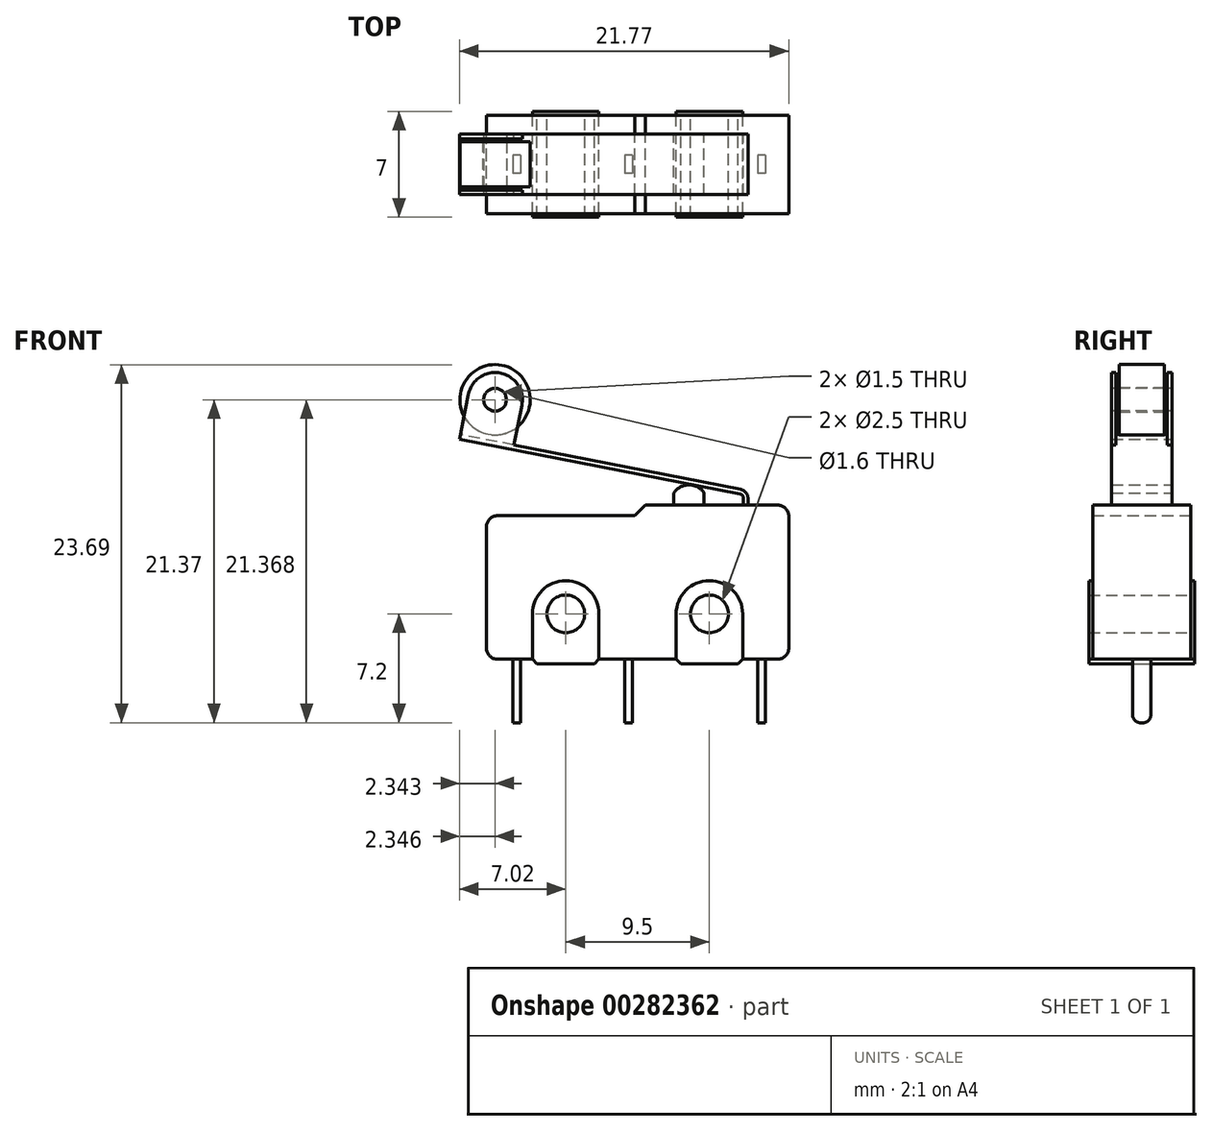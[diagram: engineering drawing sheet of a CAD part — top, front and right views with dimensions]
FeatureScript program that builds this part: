
annotation { "Feature Type Name" : "Feature", "Feature Type Description" : "" }
export const myFeature = defineFeature(function(context is Context, id is Id, definition is map)
    precondition{}
    {
        {
            var Q0;
            Q0=qCreatedBy(makeId("Front.planeOp"),FACE);
            var sketch = newSketch(context, id + "F0", { "sketchPlane" : qUnion([Q0])});
            skLineSegment(sketch, "E0.bottom", {"start": v(0.75, 0) * mm, "end": v(3.05, 0) * mm});
            skLineSegment(sketch, "E0.top", {"start": v(0.75, 9.5) * mm, "end": v(9.8, 9.5) * mm});
            skLineSegment(sketch, "E0.left", {"start": v(0, 0.75) * mm, "end": v(0, 8.75) * mm});
            skLineSegment(sketch, "E0.right", {"start": v(20, 0.75) * mm, "end": v(20, 9.45) * mm});
            skLineSegment(sketch, "E1", {"start": v(9.8, 9.5) * mm, "end": v(10.5, 10.2) * mm});
            skLineSegment(sketch, "E2", {"start": v(10.5, 10.2) * mm, "end": v(19.25, 10.2) * mm});
            skPoint(sketch, "E3.visualSharp", {"position": v(0, 9.5) * mm});
            skArc(sketch, "E3.filletArc", {"start": v(0.75, 9.5) * mm, "mid": v(0.22, 9.28) * mm, "end": v(0, 8.75) * mm});
            skPoint(sketch, "E4.visualSharp", {"position": v(20, 10.2) * mm});
            skArc(sketch, "E4.filletArc", {"start": v(20, 9.45) * mm, "mid": v(19.78, 9.98) * mm, "end": v(19.25, 10.2) * mm});
            skPoint(sketch, "E5.visualSharp", {"position": v(20, 0) * mm});
            skArc(sketch, "E5.filletArc", {"start": v(19.25, 0) * mm, "mid": v(19.78, 0.22) * mm, "end": v(20, 0.75) * mm});
            skPoint(sketch, "E6.visualSharp", {"position": v(0, 0) * mm});
            skArc(sketch, "E6.filletArc", {"start": v(0, 0.75) * mm, "mid": v(0.22, 0.22) * mm, "end": v(0.75, 0) * mm});
            skLineSegment(sketch, "E7", {"start": v(0, 3) * mm, "end": v(20, 3) * mm, "construction": true});
            skLineSegment(sketch, "E8", {"start": v(10, 3) * mm, "end": v(10, 0) * mm, "construction": true});
            skCircle(sketch, "E9", {"center": v(5.25, 3) * mm, "radius": 1.25 * mm});
            skCircle(sketch, "E10", {"center": v(14.75, 3) * mm, "radius": 1.25 * mm});
            skCircle(sketch, "E11", {"center": v(5.25, 3) * mm, "radius": 2.2 * mm, "construction": true});
            skCircle(sketch, "E12", {"center": v(14.75, 3) * mm, "radius": 2.2 * mm, "construction": true});
            skLineSegment(sketch, "E13", {"start": v(3.05, 3) * mm, "end": v(3.05, 0) * mm, "construction": true});
            skLineSegment(sketch, "E14", {"start": v(3.05, 0) * mm, "end": v(3.35, -0.3) * mm});
            skLineSegment(sketch, "E15", {"start": v(3.35, -0.3) * mm, "end": v(7.15, -0.3) * mm});
            skLineSegment(sketch, "E16", {"start": v(7.45, 3) * mm, "end": v(7.45, 0) * mm, "construction": true});
            skLineSegment(sketch, "E17", {"start": v(7.45, 0) * mm, "end": v(7.15, -0.3) * mm});
            skLineSegment(sketch, "E18.trimOffspring", {"start": v(7.45, 0) * mm, "end": v(12.55, 0) * mm});
            skLineSegment(sketch, "E19", {"start": v(12.55, 3) * mm, "end": v(12.55, 0) * mm, "construction": true});
            skLineSegment(sketch, "E20", {"start": v(12.55, 0) * mm, "end": v(12.85, -0.3) * mm});
            skLineSegment(sketch, "E21", {"start": v(12.85, -0.3) * mm, "end": v(16.65, -0.3) * mm});
            skLineSegment(sketch, "E22", {"start": v(16.95, 3) * mm, "end": v(16.95, 0) * mm, "construction": true});
            skLineSegment(sketch, "E23", {"start": v(16.95, 0) * mm, "end": v(16.65, -0.3) * mm});
            skLineSegment(sketch, "E24.trimOffspring", {"start": v(16.95, 0) * mm, "end": v(19.25, 0) * mm});
            skSolve(sketch);
        }
        {
            var Q0;
            Q0=qSketchRegion(id+"F0",true);
            extrude(context, id + "F1", {"entities" : qUnion([Q0]), "endBound" : BoundingType.SYMMETRIC, "depth" : 6.5 * mm});
        }
        {
            var Q0;
            Q0=makeQuery(id+"F1.opExtrude","CAP_FACE",FACE,{"disambiguationData":[OSD([sQuery(id+"F0.wireOp",EDGE,"E0.bottom"),sQuery(id+"F0.wireOp",EDGE,"E0.top"),sQuery(id+"F0.wireOp",EDGE,"E0.left"),sQuery(id+"F0.wireOp",EDGE,"E0.right"),sQuery(id+"F0.wireOp",EDGE,"E1"),sQuery(id+"F0.wireOp",EDGE,"E2"),sQuery(id+"F0.wireOp",EDGE,"E3.filletArc"),sQuery(id+"F0.wireOp",EDGE,"E4.filletArc"),sQuery(id+"F0.wireOp",EDGE,"E5.filletArc"),sQuery(id+"F0.wireOp",EDGE,"E6.filletArc"),sQuery(id+"F0.wireOp",EDGE,"E9"),sQuery(id+"F0.wireOp",EDGE,"E10")])],"isStart":false});
            var sketch = newSketch(context, id + "F2", { "sketchPlane" : qUnion([Q0])});
            skCircle(sketch, "E25", {"center": v(5.25, 3) * mm, "radius": 1.25 * mm});
            skArc(sketch, "E26", {"start": v(7.45, 3) * mm, "mid": v(5.25, 5.2) * mm, "end": v(3.05, 3) * mm});
            skCircle(sketch, "E27", {"center": v(14.75, 3) * mm, "radius": 1.25 * mm});
            skArc(sketch, "E28", {"start": v(16.95, 3) * mm, "mid": v(14.75, 5.2) * mm, "end": v(12.55, 3) * mm});
            skLineSegment(sketch, "E29", {"start": v(16.95, 3) * mm, "end": v(3.05, 3) * mm, "construction": true});
            skLineSegment(sketch, "E30", {"start": v(3.05, 3) * mm, "end": v(3.05, 0) * mm});
            skLineSegment(sketch, "E31", {"start": v(7.45, 3) * mm, "end": v(7.45, 0) * mm});
            skLineSegment(sketch, "E32", {"start": v(12.55, 3) * mm, "end": v(12.55, 0) * mm});
            skLineSegment(sketch, "E33", {"start": v(16.95, 3) * mm, "end": v(16.95, 0) * mm});
            skLineSegment(sketch, "E34", {"start": v(3.05, 0) * mm, "end": v(3.35, -0.3) * mm});
            skLineSegment(sketch, "E35", {"start": v(3.35, -0.3) * mm, "end": v(7.15, -0.3) * mm});
            skLineSegment(sketch, "E36", {"start": v(7.15, -0.3) * mm, "end": v(7.45, 0) * mm});
            skLineSegment(sketch, "E37", {"start": v(12.55, 0) * mm, "end": v(12.85, -0.3) * mm});
            skLineSegment(sketch, "E38", {"start": v(12.85, -0.3) * mm, "end": v(16.65, -0.3) * mm});
            skLineSegment(sketch, "E39", {"start": v(16.65, -0.3) * mm, "end": v(16.95, 0) * mm});
            skSolve(sketch);
        }
        {
            var Q0;
            Q0=qSketchRegion(id+"F2",true);
            extrude(context, id + "F3", {"entities" : qUnion([Q0]), "operationType" : NewBodyOperationType.ADD, "depth" : 0.25 * mm});
        }
        {
            var Q0;
            Q0=makeQuery(id+"F1.opExtrude","CAP_FACE",FACE,{"disambiguationData":[OSD([sQuery(id+"F0.wireOp",EDGE,"E0.bottom"),sQuery(id+"F0.wireOp",EDGE,"E0.top"),sQuery(id+"F0.wireOp",EDGE,"E0.left"),sQuery(id+"F0.wireOp",EDGE,"E0.right"),sQuery(id+"F0.wireOp",EDGE,"E1"),sQuery(id+"F0.wireOp",EDGE,"E2"),sQuery(id+"F0.wireOp",EDGE,"E3.filletArc"),sQuery(id+"F0.wireOp",EDGE,"E4.filletArc"),sQuery(id+"F0.wireOp",EDGE,"E5.filletArc"),sQuery(id+"F0.wireOp",EDGE,"E6.filletArc"),sQuery(id+"F0.wireOp",EDGE,"E9"),sQuery(id+"F0.wireOp",EDGE,"E10"),sQuery(id+"F0.wireOp",EDGE,"E14"),sQuery(id+"F0.wireOp",EDGE,"E15"),sQuery(id+"F0.wireOp",EDGE,"E17"),sQuery(id+"F0.wireOp",EDGE,"E18.trimOffspring"),sQuery(id+"F0.wireOp",EDGE,"E20"),sQuery(id+"F0.wireOp",EDGE,"E21"),sQuery(id+"F0.wireOp",EDGE,"E23"),sQuery(id+"F0.wireOp",EDGE,"E24.trimOffspring")])],"isStart":true});
            var sketch = newSketch(context, id + "F4", { "sketchPlane" : qUnion([Q0])});
            skCircle(sketch, "E40", {"center": v(-14.75, 3) * mm, "radius": 1.25 * mm});
            skArc(sketch, "E41", {"start": v(-12.55, 3) * mm, "mid": v(-14.75, 5.2) * mm, "end": v(-16.95, 3) * mm});
            skCircle(sketch, "E42", {"center": v(-5.25, 3) * mm, "radius": 1.25 * mm});
            skArc(sketch, "E43", {"start": v(-3.05, 3) * mm, "mid": v(-5.25, 5.2) * mm, "end": v(-7.45, 3) * mm});
            skLineSegment(sketch, "E44", {"start": v(-16.95, 3) * mm, "end": v(-16.95, 0) * mm});
            skLineSegment(sketch, "E45", {"start": v(-16.95, 0) * mm, "end": v(-16.65, -0.3) * mm});
            skLineSegment(sketch, "E46", {"start": v(-16.65, -0.3) * mm, "end": v(-12.85, -0.3) * mm});
            skLineSegment(sketch, "E47", {"start": v(-12.85, -0.3) * mm, "end": v(-12.55, 0) * mm});
            skLineSegment(sketch, "E48", {"start": v(-12.55, 0) * mm, "end": v(-12.55, 3) * mm});
            skLineSegment(sketch, "E49", {"start": v(-7.45, 3) * mm, "end": v(-7.45, 0) * mm});
            skLineSegment(sketch, "E50", {"start": v(-7.45, 0) * mm, "end": v(-7.15, -0.3) * mm});
            skLineSegment(sketch, "E51", {"start": v(-7.15, -0.3) * mm, "end": v(-3.35, -0.3) * mm});
            skLineSegment(sketch, "E52", {"start": v(-3.35, -0.3) * mm, "end": v(-3.05, 0) * mm});
            skLineSegment(sketch, "E53", {"start": v(-3.05, 0) * mm, "end": v(-3.05, 3) * mm});
            skSolve(sketch);
        }
        {
            var Q0;
            Q0=qSketchRegion(id+"F4",true);
            extrude(context, id + "F5", {"entities" : qUnion([Q0]), "operationType" : NewBodyOperationType.ADD, "depth" : 0.25 * mm});
        }
        {
            var Q0;
            Q0=qCreatedBy(makeId("Front.planeOp"),FACE);
            var sketch = newSketch(context, id + "F6", { "sketchPlane" : qUnion([Q0])});
            skLineSegment(sketch, "E54", {"start": v(0, 0) * mm, "end": v(0, 10.2) * mm, "construction": true});
            skLineSegment(sketch, "E55", {"start": v(0, 10.2) * mm, "end": v(17, 10.2) * mm, "construction": true});
            skLineSegment(sketch, "E56", {"start": v(14.4, 10.2) * mm, "end": v(14.4, 11) * mm});
            skLineSegment(sketch, "E57", {"start": v(14.4, 10.2) * mm, "end": v(12.4, 10.2) * mm});
            skLineSegment(sketch, "E58", {"start": v(12.4, 10.2) * mm, "end": v(12.4, 11) * mm});
            skArc(sketch, "E59", {"start": v(14.4, 11) * mm, "mid": v(13.4, 11.54) * mm, "end": v(12.4, 11) * mm});
            skLineSegment(sketch, "E60", {"start": v(17, 10.2) * mm, "end": v(17, 10.65) * mm});
            skLineSegment(sketch, "E61", {"start": v(16.76, 10.95) * mm, "end": v(-1.77, 14.57) * mm});
            skPoint(sketch, "E62.visualSharp", {"position": v(17, 10.9) * mm});
            skArc(sketch, "E62.filletArc", {"start": v(17, 10.65) * mm, "mid": v(16.93, 10.84) * mm, "end": v(16.76, 10.95) * mm});
            skLineSegment(sketch, "E63.0", {"start": v(16.82, 11.24) * mm, "end": v(1.82, 14.17) * mm});
            skArc(sketch, "E63.1", {"start": v(17.3, 10.65) * mm, "mid": v(17.16, 11.03) * mm, "end": v(16.82, 11.24) * mm});
            skLineSegment(sketch, "E63.2", {"start": v(17.3, 10.2) * mm, "end": v(17.3, 10.65) * mm});
            skLineSegment(sketch, "E64", {"start": v(17, 10.2) * mm, "end": v(17.3, 10.2) * mm});
            skLineSegment(sketch, "E65", {"start": v(0, 14.22) * mm, "end": v(0.58, 17.17) * mm, "construction": true});
            skArc(sketch, "E66", {"start": v(2.34, 16.82) * mm, "mid": v(0.92, 18.93) * mm, "end": v(-1.2, 17.51) * mm});
            skLineSegment(sketch, "E67", {"start": v(0.58, 17.17) * mm, "end": v(2.34, 16.82) * mm, "construction": true});
            skLineSegment(sketch, "E68", {"start": v(2.34, 16.82) * mm, "end": v(1.82, 14.17) * mm});
            skLineSegment(sketch, "E69", {"start": v(0.58, 17.17) * mm, "end": v(-1.2, 17.51) * mm, "construction": true});
            skLineSegment(sketch, "E70", {"start": v(-1.2, 17.51) * mm, "end": v(-1.77, 14.57) * mm});
            skCircle(sketch, "E71", {"center": v(0.58, 17.17) * mm, "radius": 0.75 * mm});
            skSolve(sketch);
        }
        {
            var Q0;
            Q0=qSketchRegion(id+"F6",true);
            extrude(context, id + "F7", {"entities" : qUnion([Q0]), "operationType" : NewBodyOperationType.ADD, "endBound" : BoundingType.SYMMETRIC, "depth" : 4 * mm});
        }
        {
            var Q0;
            Q0=makeQuery(id+"F7.opExtrude","SWEPT_FACE",FACE,{"disambiguationData":[OSD([sQuery(id+"F6.wireOp",EDGE,"E70")])]});
            var sketch = newSketch(context, id + "F8", { "sketchPlane" : qUnion([Q0])});
            skLineSegment(sketch, "E72.bottom", {"start": v(-1.7, 14.26) * mm, "end": v(1.7, 14.26) * mm});
            skLineSegment(sketch, "E72.top", {"start": v(-1.7, 20.26) * mm, "end": v(1.7, 20.26) * mm});
            skLineSegment(sketch, "E72.left", {"start": v(-1.7, 14.26) * mm, "end": v(-1.7, 20.26) * mm});
            skLineSegment(sketch, "E72.right", {"start": v(1.7, 14.26) * mm, "end": v(1.7, 20.26) * mm});
            skSolve(sketch);
        }
        {
            var Q0;
            Q0=qSketchRegion(id+"F8",true);
            extrude(context, id + "F9", {"entities" : qUnion([Q0]), "operationType" : NewBodyOperationType.REMOVE, "oppositeDirection" : true, "depth" : 25 * mm});
        }
        {
            var Q0;
            Q0=makeQuery(id+"F7.opExtrude","CAP_FACE",FACE,{"disambiguationData":[OSD([sQuery(id+"F6.wireOp",EDGE,"E60"),sQuery(id+"F6.wireOp",EDGE,"E61"),sQuery(id+"F6.wireOp",EDGE,"E62.filletArc"),sQuery(id+"F6.wireOp",EDGE,"E63.0"),sQuery(id+"F6.wireOp",EDGE,"E63.1"),sQuery(id+"F6.wireOp",EDGE,"E63.2"),sQuery(id+"F6.wireOp",EDGE,"E64"),sQuery(id+"F6.wireOp",EDGE,"E66"),sQuery(id+"F6.wireOp",EDGE,"E68"),sQuery(id+"F6.wireOp",EDGE,"E70"),sQuery(id+"F6.wireOp",EDGE,"E71")])],"isStart":false});
            var sketch = newSketch(context, id + "F10", { "sketchPlane" : qUnion([Q0])});
            skCircle(sketch, "E73", {"center": v(0.58, 17.17) * mm, "radius": 0.75 * mm});
            skSolve(sketch);
        }
        {
            var Q0;
            Q0=qSketchRegion(id+"F10",true);
            extrude(context, id + "F11", {"entities" : qUnion([Q0]), "oppositeDirection" : true, "depth" : 4 * mm});
        }
        {
            var Q0;
            Q0=makeQuery(id+"F1.opExtrude","SWEPT_FACE",FACE,{"disambiguationData":[OSD([sQuery(id+"F0.wireOp",EDGE,"E18.trimOffspring")])]});
            var sketch = newSketch(context, id + "F12", { "sketchPlane" : qUnion([Q0])});
            skLineSegment(sketch, "E74", {"start": v(0, 0) * mm, "end": v(18.2, 0) * mm, "construction": true});
            skLineSegment(sketch, "E75.bottom", {"start": v(18.45, -0.6) * mm, "end": v(17.95, -0.6) * mm});
            skLineSegment(sketch, "E75.top", {"start": v(18.45, 0.6) * mm, "end": v(17.95, 0.6) * mm});
            skLineSegment(sketch, "E75.left", {"start": v(18.45, -0.6) * mm, "end": v(18.45, 0.6) * mm});
            skLineSegment(sketch, "E75.right", {"start": v(17.95, -0.6) * mm, "end": v(17.95, 0.6) * mm});
            skPoint(sketch, "E75.middle", {"position": v(18.2, 0) * mm});
            skLineSegment(sketch, "E76.bottom", {"start": v(9.65, -0.6) * mm, "end": v(9.15, -0.6) * mm});
            skLineSegment(sketch, "E76.top", {"start": v(9.65, 0.6) * mm, "end": v(9.15, 0.6) * mm});
            skLineSegment(sketch, "E76.left", {"start": v(9.65, -0.6) * mm, "end": v(9.65, 0.6) * mm});
            skLineSegment(sketch, "E76.right", {"start": v(9.15, -0.6) * mm, "end": v(9.15, 0.6) * mm});
            skPoint(sketch, "E76.middle", {"position": v(9.4, 0) * mm});
            skLineSegment(sketch, "E77.bottom", {"start": v(2.25, -0.6) * mm, "end": v(1.75, -0.6) * mm});
            skLineSegment(sketch, "E77.top", {"start": v(2.25, 0.6) * mm, "end": v(1.75, 0.6) * mm});
            skLineSegment(sketch, "E77.left", {"start": v(2.25, -0.6) * mm, "end": v(2.25, 0.6) * mm});
            skLineSegment(sketch, "E77.right", {"start": v(1.75, -0.6) * mm, "end": v(1.75, 0.6) * mm});
            skPoint(sketch, "E77.middle", {"position": v(2, 0) * mm});
            skSolve(sketch);
        }
        {
            var Q0;
            Q0=qSketchRegion(id+"F12",true);
            extrude(context, id + "F13", {"entities" : qUnion([Q0]), "operationType" : NewBodyOperationType.ADD, "depth" : 4.2 * mm});
        }
        {
            var Q0;
            Q0=makeQuery(id+"F13.opExtrude","CAP_EDGE",EDGE,{"disambiguationData":[OSD([sQuery(id+"F12.wireOp",EDGE,"E77.top")])],"isStart":false});
            var Q1;
            Q1=makeQuery(id+"F13.opExtrude","CAP_EDGE",EDGE,{"disambiguationData":[OSD([sQuery(id+"F12.wireOp",EDGE,"E77.bottom")])],"isStart":false});
            var Q2;
            Q2=makeQuery(id+"F13.opExtrude","CAP_EDGE",EDGE,{"disambiguationData":[OSD([sQuery(id+"F12.wireOp",EDGE,"E76.bottom")])],"isStart":false});
            var Q3;
            Q3=makeQuery(id+"F13.opExtrude","CAP_EDGE",EDGE,{"disambiguationData":[OSD([sQuery(id+"F12.wireOp",EDGE,"E76.top")])],"isStart":false});
            var Q4;
            Q4=makeQuery(id+"F13.opExtrude","CAP_EDGE",EDGE,{"disambiguationData":[OSD([sQuery(id+"F12.wireOp",EDGE,"E75.top")])],"isStart":false});
            var Q5;
            Q5=makeQuery(id+"F13.opExtrude","CAP_EDGE",EDGE,{"disambiguationData":[OSD([sQuery(id+"F12.wireOp",EDGE,"E75.bottom")])],"isStart":false});
            fillet(context, id + "F14", {"entities" : qUnion([Q0, Q1, Q2, Q3, Q4, Q5]), "radius" : 0.5 * mm, "tangentPropagation" : true, "allowEdgeOverflow" : false});
        }
        {
            var Q0;
            Q0=qCreatedBy(makeId("Front.planeOp"),FACE);
            var sketch = newSketch(context, id + "F15", { "sketchPlane" : qUnion([Q0])});
            skLineSegment(sketch, "E78", {"start": v(0, 0) * mm, "end": v(0, 14.22) * mm, "construction": true});
            skLineSegment(sketch, "E79", {"start": v(0, 14.22) * mm, "end": v(0.57, 17.17) * mm, "construction": true});
            skLineSegment(sketch, "E80", {"start": v(0, 14.22) * mm, "end": v(1.5, 13.93) * mm, "construction": true});
            skCircle(sketch, "E81", {"center": v(0.57, 17.17) * mm, "radius": 0.8 * mm});
            skCircle(sketch, "E82", {"center": v(0.57, 17.17) * mm, "radius": 2.33 * mm});
            skSolve(sketch);
        }
        {
            var Q0;
            Q0=qSketchRegion(id+"F15",true);
            extrude(context, id + "F16", {"entities" : qUnion([Q0]), "endBound" : BoundingType.SYMMETRIC, "depth" : 3 * mm});
        }
    });
